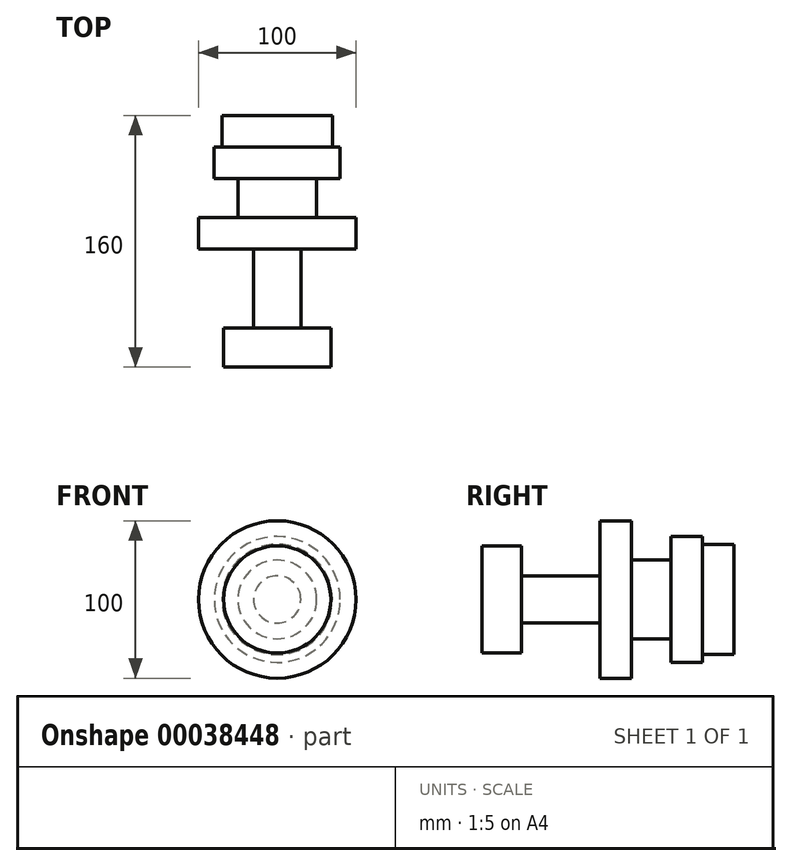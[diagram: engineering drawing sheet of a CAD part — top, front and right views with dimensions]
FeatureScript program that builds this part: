
annotation { "Feature Type Name" : "Feature", "Feature Type Description" : "" }
export const myFeature = defineFeature(function(context is Context, id is Id, definition is map)
    precondition{}
    {
        {
            var Q0;
            Q0=qCreatedBy(makeId("Front.planeOp"),FACE);
            var sketch = newSketch(context, id + "F0", { "sketchPlane" : qUnion([Q0])});
            skCircle(sketch, "E0", {"center": v(0, 0) * mm, "radius": 35 * mm});
            skSolve(sketch);
        }
        {
            var Q0;
            Q0 = qSketchRegion(id + "F0", true);
            extrude(context, id + "F1", {"entities" : qUnion([Q0]), "depth" : 20 * mm});
        }
        {
            var Q0;
            Q0=makeQuery(id+"F1.opExtrude","CAP_FACE",FACE,{"disambiguationData":[OSD([sQuery(id+"F0.wireOp",EDGE,"E0")])],"isStart":false});
            var sketch = newSketch(context, id + "F2", { "sketchPlane" : qUnion([Q0])});
            skCircle(sketch, "E1", {"center": v(0, 0) * mm, "radius": 40 * mm});
            skSolve(sketch);
        }
        {
            var Q0;
            Q0=makeQuery(id+"F2.imprint","IMPRINT",FACE,{"disambiguationData":[TD([[makeQuery(id+"F2.imprint","IMPRINT",EDGE,{"derivedFrom":sQuery(id+"F2.wireOp",EDGE,"E1")}),1.0]])]});
            var Q1;
            Q1=makeQuery(id+"F2.imprint","IMPRINT",FACE,{"disambiguationData":[TD([[makeQuery(id+"F2.imprint","IMPRINT",EDGE,{"derivedFrom":makeQuery(id+"F1.opExtrude","CAP_EDGE",EDGE,{"disambiguationData":[OSD([sQuery(id+"F0.wireOp",EDGE,"E0")])],"isStart":false})}),1.0]])]});
            var Q2;
            Q2=sQuery(id+"F2.wireOp",EDGE,"E1");
            extrude(context, id + "F3", {"entities" : qUnion([Q0, Q1]), "surfaceEntities" : qUnion([Q2]), "depth" : 20 * mm});
        }
        {
            var Q0;
            Q0=makeQuery(id+"F3.opExtrude","CAP_FACE",FACE,{"disambiguationData":[OSD([sQuery(id+"F2.wireOp",EDGE,"E1")])],"isStart":false});
            var sketch = newSketch(context, id + "F4", { "sketchPlane" : qUnion([Q0])});
            skCircle(sketch, "E2", {"center": v(0, 0) * mm, "radius": 25 * mm});
            skSolve(sketch);
        }
        {
            var Q0;
            Q0=makeQuery(id+"F4.imprint","IMPRINT",FACE,{"disambiguationData":[TD([[makeQuery(id+"F4.imprint","IMPRINT",EDGE,{"derivedFrom":sQuery(id+"F4.wireOp",EDGE,"E2")}),1.0]])]});
            var Q1;
            Q1=sQuery(id+"F4.wireOp",EDGE,"E2");
            extrude(context, id + "F5", {"entities" : qUnion([Q0]), "operationType" : NewBodyOperationType.ADD, "surfaceEntities" : qUnion([Q1]), "depth" : 25 * mm});
        }
        {
            var Q0;
            Q0=makeQuery(id+"F5.opExtrude","CAP_FACE",FACE,{"disambiguationData":[OSD([sQuery(id+"F4.wireOp",EDGE,"E2")])],"isStart":false});
            var sketch = newSketch(context, id + "F6", { "sketchPlane" : qUnion([Q0])});
            skCircle(sketch, "E3", {"center": v(0, 0) * mm, "radius": 50 * mm});
            skSolve(sketch);
        }
        {
            var Q0;
            Q0 = qSketchRegion(id + "F6", true);
            extrude(context, id + "F7", {"entities" : qUnion([Q0]), "operationType" : NewBodyOperationType.ADD, "depth" : 20 * mm});
        }
        {
            var Q0;
            Q0=makeQuery(id+"F7.opExtrude","CAP_FACE",FACE,{"disambiguationData":[OSD([sQuery(id+"F6.wireOp",EDGE,"E3")])],"isStart":false});
            var sketch = newSketch(context, id + "F8", { "sketchPlane" : qUnion([Q0])});
            skCircle(sketch, "E4", {"center": v(0, 0) * mm, "radius": 15 * mm});
            skSolve(sketch);
        }
        {
            var Q0;
            Q0 = qSketchRegion(id + "F8", true);
            extrude(context, id + "F9", {"entities" : qUnion([Q0]), "operationType" : NewBodyOperationType.ADD, "depth" : 50 * mm});
        }
        {
            var Q0;
            Q0=makeQuery(id+"F9.opExtrude","CAP_FACE",FACE,{"disambiguationData":[OSD([sQuery(id+"F8.wireOp",EDGE,"E4")])],"isStart":false});
            var sketch = newSketch(context, id + "F10", { "sketchPlane" : qUnion([Q0])});
            skCircle(sketch, "E5", {"center": v(0, 0) * mm, "radius": 34.03 * mm});
            skSolve(sketch);
        }
        {
            var Q0;
            Q0=makeQuery(id+"F10.imprint","IMPRINT",FACE,{"disambiguationData":[TD([[makeQuery(id+"F10.imprint","IMPRINT",EDGE,{"derivedFrom":makeQuery(id+"F9.opExtrude","CAP_EDGE",EDGE,{"disambiguationData":[OSD([sQuery(id+"F8.wireOp",EDGE,"E4")])],"isStart":false})}),1.0]])]});
            var Q1;
            Q1=makeQuery(id+"F10.imprint","IMPRINT",FACE,{"disambiguationData":[TD([[makeQuery(id+"F10.imprint","IMPRINT",EDGE,{"derivedFrom":sQuery(id+"F10.wireOp",EDGE,"E5")}),1.0]])]});
            var Q2;
            Q2=sQuery(id+"F10.wireOp",EDGE,"E5");
            extrude(context, id + "F11", {"entities" : qUnion([Q0, Q1]), "operationType" : NewBodyOperationType.ADD, "surfaceEntities" : qUnion([Q2]), "depth" : 25 * mm});
        }
    });
